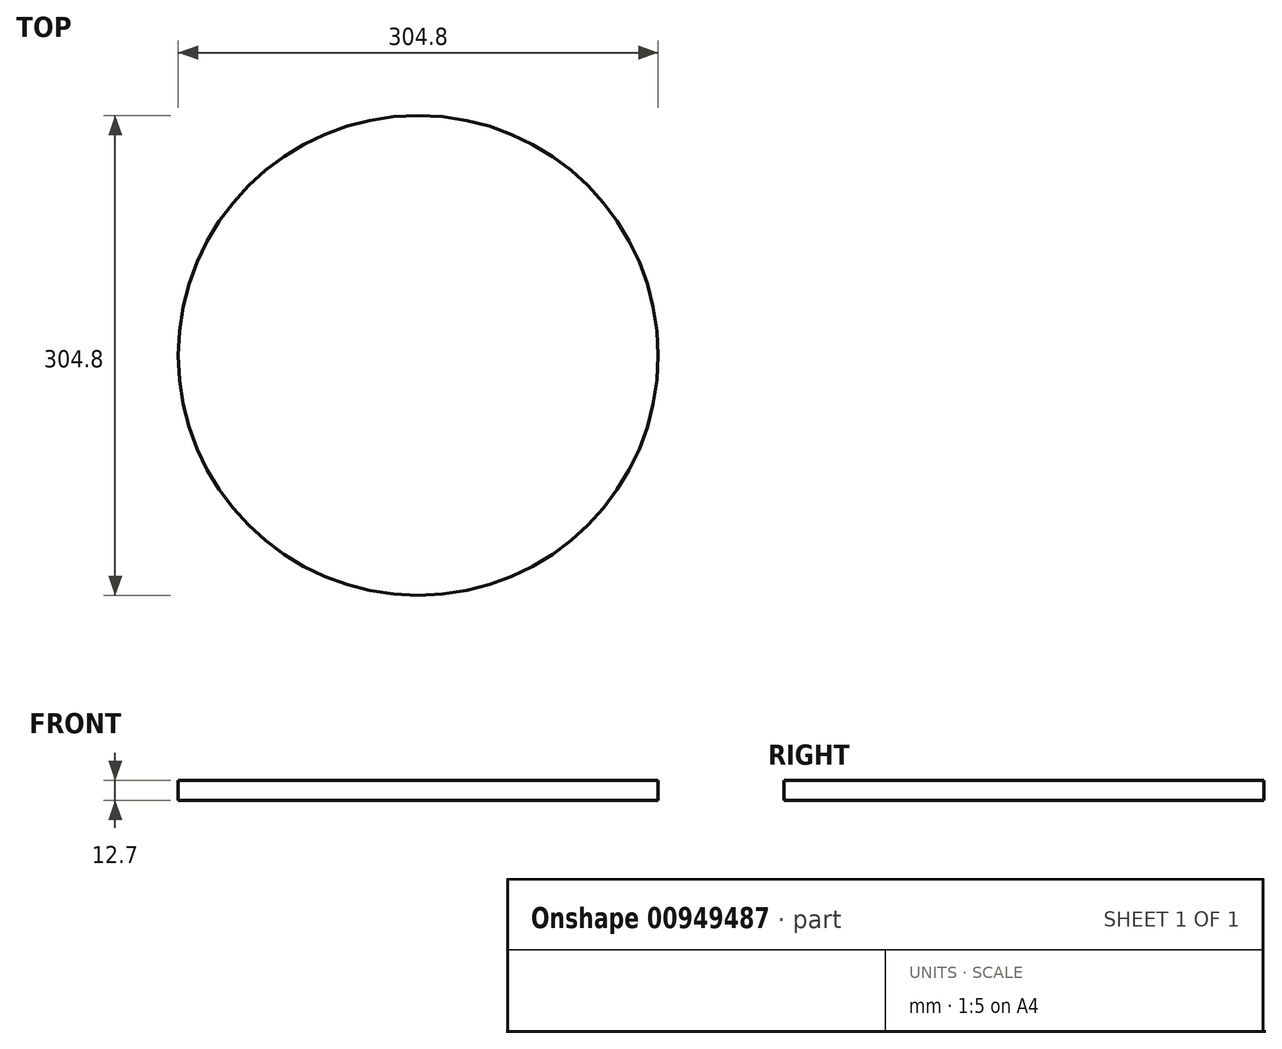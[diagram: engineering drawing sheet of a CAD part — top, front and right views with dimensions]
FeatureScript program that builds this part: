
annotation { "Feature Type Name" : "Feature", "Feature Type Description" : "" }
export const myFeature = defineFeature(function(context is Context, id is Id, definition is map)
    precondition{}
    {
        {
            var Q0;
            Q0=qCreatedBy(makeId("Top.planeOp"),FACE);
            var sketch = newSketch(context, id + "F0", { "sketchPlane" : qUnion([Q0])});
            skCircle(sketch, "E0", {"center": v(0, 0) * mm, "radius": 152.4 * mm});
            skSolve(sketch);
        }
        {
            var Q0;
            Q0=makeQuery(id+"F0.imprint","IMPRINT",FACE,{"disambiguationData":[TD([[makeQuery(id+"F0.imprint","IMPRINT",EDGE,{"derivedFrom":sQuery(id+"F0.wireOp",EDGE,"E0")}),1.0]])]});
            extrude(context, id + "F1", {"entities" : qUnion([Q0]), "depth" : 12.7 * mm, "offsetDistance" : 25.4 * mm});
        }
    });
